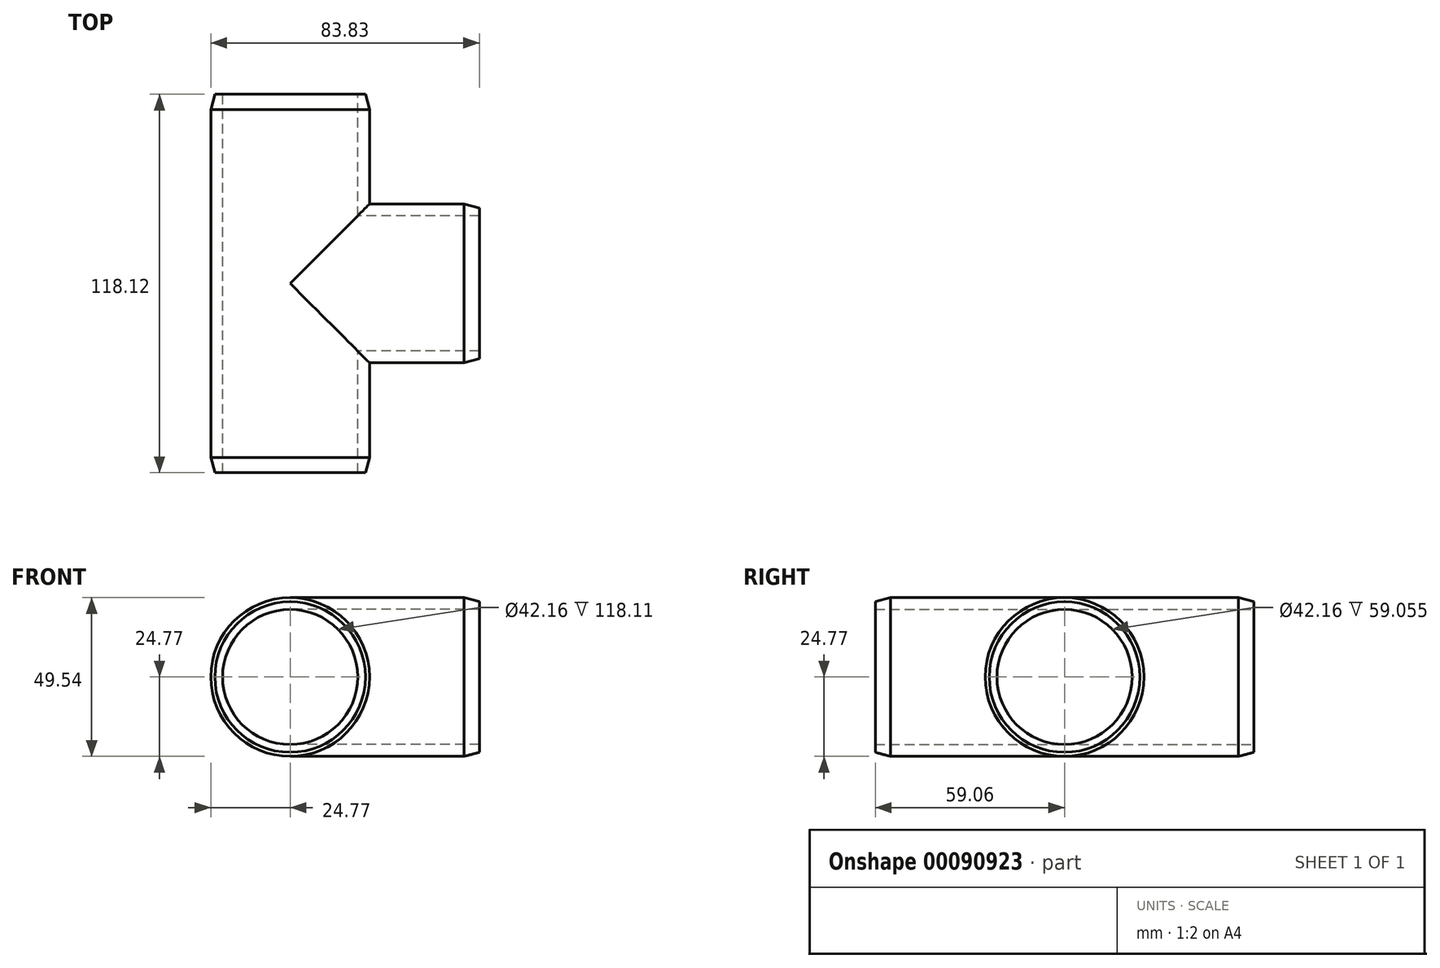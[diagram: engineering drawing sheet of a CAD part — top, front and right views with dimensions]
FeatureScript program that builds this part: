
annotation { "Feature Type Name" : "Feature", "Feature Type Description" : "" }
export const myFeature = defineFeature(function(context is Context, id is Id, definition is map)
    precondition{}
    {
        {
            var Q0;
            Q0=qCreatedBy(makeId("Front.planeOp"),FACE);
            var sketch = newSketch(context, id + "F0", { "sketchPlane" : qUnion([Q0])});
            skCircle(sketch, "E0", {"center": v(0, 0) * mm, "radius": 21.08 * mm});
            skCircle(sketch, "E1.0", {"center": v(0, 0) * mm, "radius": 24.77 * mm});
            skSolve(sketch);
        }
        {
            var Q0;
            Q0=qSketchRegion(id+"F0",true);
            extrude(context, id + "F1", {"entities" : qUnion([Q0]), "endBound" : BoundingType.SYMMETRIC, "depth" : 118.11 * mm});
        }
        {
            var Q0;
            Q0=qCreatedBy(makeId("Right.planeOp"),FACE);
            var sketch = newSketch(context, id + "F2", { "sketchPlane" : qUnion([Q0])});
            skCircle(sketch, "E2", {"center": v(0, 0) * mm, "radius": 21.08 * mm});
            skCircle(sketch, "E3.0", {"center": v(0, 0) * mm, "radius": 24.77 * mm});
            skSolve(sketch);
        }
        {
            var Q0;
            Q0=qSketchRegion(id+"F2",true);
            extrude(context, id + "F3", {"entities" : qUnion([Q0]), "operationType" : NewBodyOperationType.ADD, "depth" : 59.05 * mm});
        }
        {
            var Q0;
            Q0=makeQuery(id+"F2.imprint","IMPRINT",FACE,{"disambiguationData":[TD([[makeQuery(id+"F2.imprint","IMPRINT",EDGE,{"derivedFrom":sQuery(id+"F2.wireOp",EDGE,"E2")}),1.0]])]});
            extrude(context, id + "F4", {"entities" : qUnion([Q0]), "operationType" : NewBodyOperationType.REMOVE, "endBound" : BoundingType.THROUGH_ALL, "depth" : 25.4 * mm});
        }
        {
            var Q0;
            Q0=makeQuery(id+"F0.imprint","IMPRINT",FACE,{"disambiguationData":[TD([[makeQuery(id+"F0.imprint","IMPRINT",EDGE,{"derivedFrom":sQuery(id+"F0.wireOp",EDGE,"E0")}),1.0]])]});
            extrude(context, id + "F5", {"entities" : qUnion([Q0]), "operationType" : NewBodyOperationType.REMOVE, "endBound" : BoundingType.THROUGH_ALL, "depth" : 25.4 * mm, "hasSecondDirection" : true, "secondDirectionBound" : SecondDirectionBoundingType.THROUGH_ALL, "secondDirectionOppositeDirection" : true, "secondDirectionDepth" : 25.4 * mm});
        }
        {
            var Q0;
            Q0=makeQuery(id+"FafeMV82ZdMxNU9_1.opExtrude","CAP_EDGE",EDGE,{"disambiguationData":[OSD([sQuery(id+"FKzl36Kfq815hOB_1.wireOp",EDGE,"0c5890f9-7e0d-4e56-9e25-773390a1f3e3.0")])],"isStart":false});
            var Q1;
            Q1=makeQuery(id+"F1.opExtrude","CAP_EDGE",EDGE,{"disambiguationData":[OSD([sQuery(id+"F0.wireOp",EDGE,"E1.0")])],"isStart":false});
            var Q2;
            Q2=makeQuery(id+"F3.opExtrude","CAP_EDGE",EDGE,{"disambiguationData":[OSD([sQuery(id+"F2.wireOp",EDGE,"E3.0")])],"isStart":false});
            chamfer(context, id + "F6", {"entities" : qUnion([Q0, Q1, Q2]), "chamferType" : ChamferType.OFFSET_ANGLE, "width" : 1.27 * mm, "oppositeDirection" : false, "angle" : 75 * degree, "tangentPropagation" : true});
        }
        {
            var Q0;
            Q0=makeQuery(id+"F1.opExtrude","CAP_EDGE",EDGE,{"disambiguationData":[OSD([sQuery(id+"F0.wireOp",EDGE,"E1.0")])],"isStart":true});
            chamfer(context, id + "F7", {"entities" : qUnion([Q0]), "chamferType" : ChamferType.OFFSET_ANGLE, "width" : 1.27 * mm, "oppositeDirection" : true, "angle" : 75 * degree, "tangentPropagation" : true});
        }
    });
